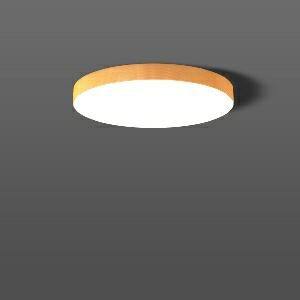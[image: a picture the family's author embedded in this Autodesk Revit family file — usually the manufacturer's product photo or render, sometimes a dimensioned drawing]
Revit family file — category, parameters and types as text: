
# Revit family: flatliner_slim_312287_002_1_76_52fd
name_source: partatom
category: Lighting Fixtures
units: mm (PartAtom-declared; Revit-internal decimal feet)

## family parameters
Cut with Voids When Loaded = No
Host = Face
Light Source = No
Part Type = Normal
Room Calculation Point = No
Round Connector Dimension = Use Diameter
Shared = No

## types (1)
- 982559.002 (1 x LED Modul 840, 3000 lm, 4000)
    Apparent Load = 38 VA
    CIE Flux Codes = 45 76 94 95 100
    Color Rendering = 80
    Color Temperature = 4000
    Default Elevation = 1800 mm
    Description = Series: FLATLINER SLIM
Decorative ceiling luminaire for interior decoration. Base luminaire prepared for the installation of fabric lampshade. Base: metal, white, powder-coated. TouchDim sensor capable. Light and/or presence sensors can be integrated. Modular design: with the basic luminaire, a cylindrical fabric lampshade with a polycarbonate satin-finish diffuser must always be ordered separately. Fabric lampshade and diffuser can be assembled without the use of tools. 
Colour: white
Diameter: 596 mm
Height: 34 mm
Lamp: LED exchangeable
Socket: without socket
Colour temperature: 4000K
Colour rendering index (CRI): 83
System power: 38 W
Rated luminous flux: 3000 lm
Beam angle Down: 117°
Luminous efficiency: 79 lm/W
Control gear: AC power, DALI dimmable
Protection class: I
Type of protection: IP 20
    Height = 34 mm  [stored 0.111549 ft]
    Lamp = 1 x LED Modul 840
    Lamp Light Flux = 3000 lm
    Lamp count = 1
    Length = 596 mm
    Lifetime = 50000 h
    Luminous efficacy = 79 lm/W
    Manufacturer = RZB
    ModVariant = No
    Model = 312287.002.1.76
    Mounting Place = Ceiling
    Mounting Type = Surface mounted
    Number of Poles = 1
    OnlyDefault = Yes
    Power Factor = 1
    Product Name = FLATLINER SLIM
    Product group = Surface mounted ceiling Fabric lampshade luminaires
    ProductGroupID = 313
    Protection Class = Protection class I
    Protection Degree = IP 20
    RLX_Detail_Level = 1
    RLX_Emergency_Light_Flux = 0 lm
    RLX_Emergency_Type = 0
    RLX_Emergency_Type_DB = No
    RlxData = <blob elided: 23981 chars, md5=341ea339>
    Socket = socket
    Standby Power = 0 W
    System Light Flux = 3000 lm
    System Power = 38 W
    Type Image = 312287.002_982442.0063_982444.002.jpg
    URL = http://relux.com
    VarID = 982559_002_a29f
    Voltage = 230 V
    Voltage Range = 220-240 V
    Weight = 0.00 kg
    Width = 0 mm  [stored 0 ft]

note: [stored X ft] marks values corroborated as IEEE doubles in the binary element streams (Revit-internal decimal feet)

## geometry (parser evidence)
native form markers: Blend x4, Sweep x12
no freeform markers — native parametric forms only
